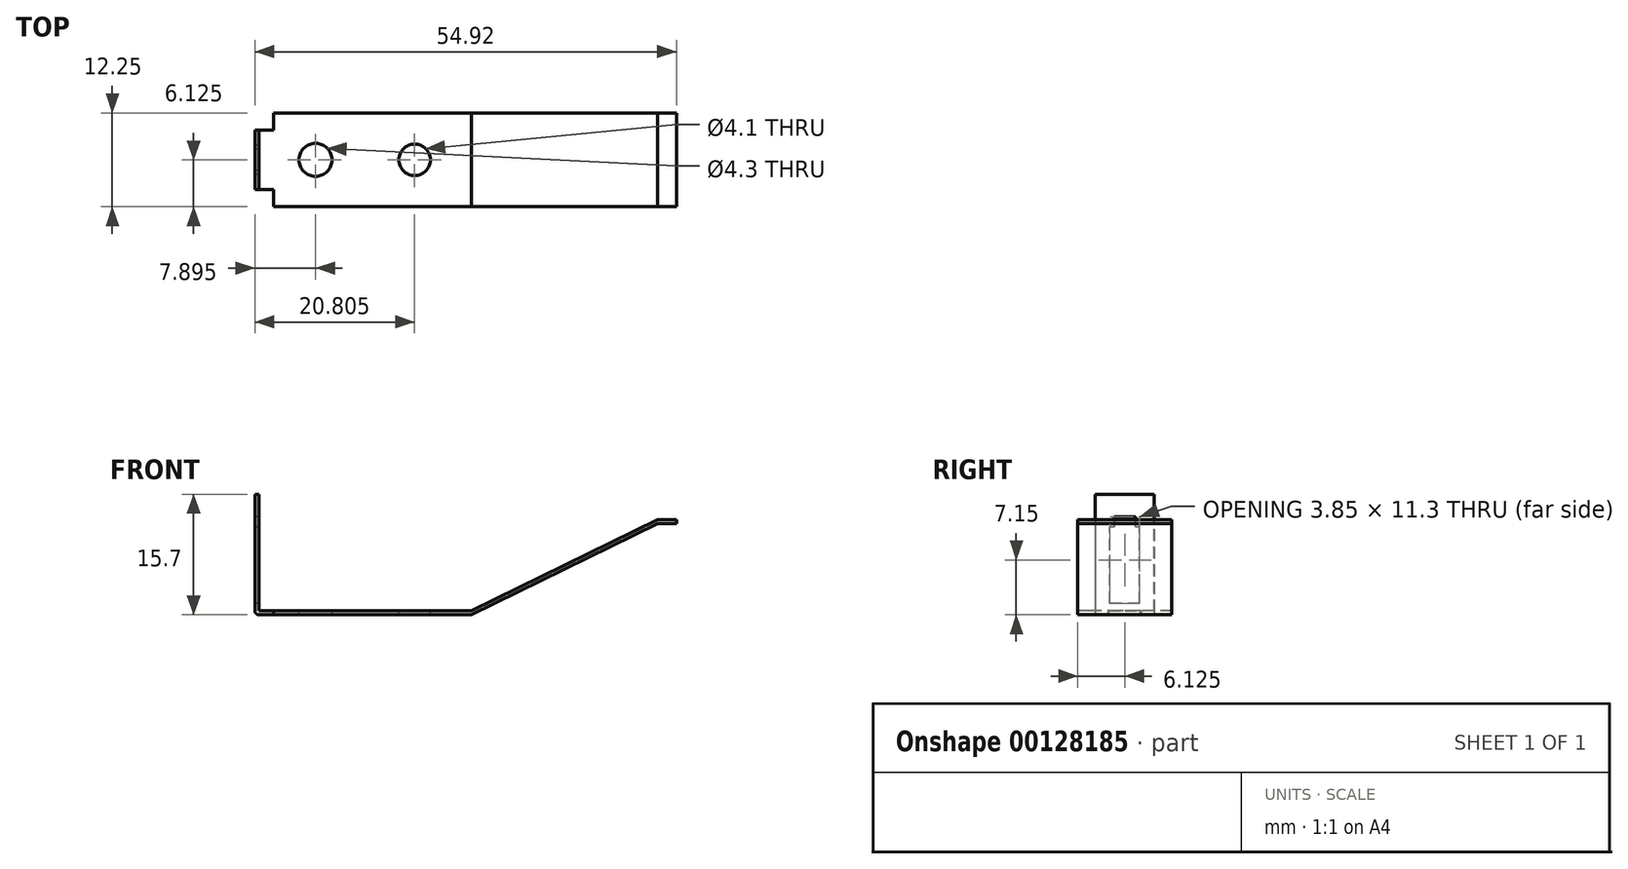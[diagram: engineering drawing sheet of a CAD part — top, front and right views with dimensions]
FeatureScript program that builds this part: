
annotation { "Feature Type Name" : "Feature", "Feature Type Description" : "" }
export const myFeature = defineFeature(function(context is Context, id is Id, definition is map)
    precondition{}
    {
        {
            var Q0;
            Q0=qCreatedBy(makeId("Front.planeOp"),FACE);
            var sketch = newSketch(context, id + "F0", { "sketchPlane" : qUnion([Q0])});
            skLineSegment(sketch, "E0", {"start": v(-12.88, 0) * mm, "end": v(12.88, 0) * mm});
            skLineSegment(sketch, "E1", {"start": v(12.88, 0) * mm, "end": v(37.16, 11.92) * mm});
            skLineSegment(sketch, "E2", {"start": v(37.16, 11.92) * mm, "end": v(39.6, 11.92) * mm});
            skLineSegment(sketch, "E3", {"start": v(-12.88, 0) * mm, "end": v(-12.88, 0.5) * mm});
            skLineSegment(sketch, "E4", {"start": v(-12.88, 0.5) * mm, "end": v(12.88, 0.5) * mm});
            skLineSegment(sketch, "E5", {"start": v(12.88, 0.5) * mm, "end": v(37.16, 12.42) * mm});
            skLineSegment(sketch, "E6", {"start": v(37.16, 12.42) * mm, "end": v(39.6, 12.42) * mm});
            skLineSegment(sketch, "E7", {"start": v(39.6, 12.42) * mm, "end": v(39.6, 11.92) * mm});
            skSolve(sketch);
        }
        {
            var Q0;
            Q0=makeQuery(id+"F0.imprint","IMPRINT",FACE,{"disambiguationData":[TD([[makeQuery(id+"F0.imprint","IMPRINT",EDGE,{"derivedFrom":sQuery(id+"F0.wireOp",EDGE,"E0")}),1.0]])]});
            extrude(context, id + "F1", {"entities" : qUnion([Q0]), "oppositeDirection" : true, "depth" : 12.25 * mm});
        }
        {
            var Q0;
            Q0=qCreatedBy(makeId("Top.planeOp"),FACE);
            var sketch = newSketch(context, id + "F2", { "sketchPlane" : qUnion([Q0])});
            skLineSegment(sketch, "E8", {"start": v(-12.88, 2.28) * mm, "end": v(-15.32, 2.28) * mm});
            skLineSegment(sketch, "E9", {"start": v(-12.88, 2.28) * mm, "end": v(-12.88, 2.28) * mm});
            skLineSegment(sketch, "E10", {"start": v(-12.88, 2.28) * mm, "end": v(-12.88, 9.97) * mm});
            skLineSegment(sketch, "E11", {"start": v(-12.88, 9.97) * mm, "end": v(-15.32, 9.97) * mm});
            skLineSegment(sketch, "E12", {"start": v(-15.32, 9.97) * mm, "end": v(-15.32, 2.28) * mm});
            skSolve(sketch);
        }
        {
            var Q0;
            Q0=makeQuery(id+"F2.imprint","IMPRINT",FACE,{"disambiguationData":[TD([[makeQuery(id+"F2.imprint","IMPRINT",EDGE,{"derivedFrom":sQuery(id+"F2.wireOp",EDGE,"E8")}),-1.0]])]});
            extrude(context, id + "F3", {"entities" : qUnion([Q0]), "operationType" : NewBodyOperationType.ADD, "depth" : 0.5 * mm});
        }
        {
            var Q0;
            Q0=qCreatedBy(makeId("Right.planeOp"),FACE);
            cPlane(context, id + "F4", {"entities" : qUnion([Q0]), "cplaneType" : CPlaneType.OFFSET, "offset" : 15.32 * mm, "oppositeDirection" : true, "width" : 150 * mm, "height" : 150 * mm});
        }
        {
            var Q0;
            Q0=qCreatedBy(id+"F4.planeOp",FACE);
            var sketch = newSketch(context, id + "F5", { "sketchPlane" : qUnion([Q0])});
            skLineSegment(sketch, "E13.0", {"start": v(9.97, 0.5) * mm, "end": v(2.28, 0.5) * mm});
            skLineSegment(sketch, "E13.1", {"start": v(9.97, 0.5) * mm, "end": v(9.97, 0) * mm});
            skLineSegment(sketch, "E13.2", {"start": v(9.97, 0) * mm, "end": v(2.28, 0) * mm});
            skLineSegment(sketch, "E13.3", {"start": v(2.28, 0.5) * mm, "end": v(2.28, 0) * mm});
            skLineSegment(sketch, "E14", {"start": v(9.97, 0) * mm, "end": v(9.97, 16) * mm});
            skLineSegment(sketch, "E15", {"start": v(9.97, 16) * mm, "end": v(2.28, 16) * mm});
            skLineSegment(sketch, "E16", {"start": v(2.28, 16) * mm, "end": v(2.28, 0) * mm});
            skLineSegment(sketch, "E17", {"start": v(8.05, 1.5) * mm, "end": v(4.2, 1.5) * mm});
            skLineSegment(sketch, "E18", {"start": v(4.2, 1.5) * mm, "end": v(4.2, 11.42) * mm});
            skLineSegment(sketch, "E19", {"start": v(8.05, 1.5) * mm, "end": v(8.05, 11.42) * mm});
            skLineSegment(sketch, "E20", {"start": v(8.05, 11.42) * mm, "end": v(4.2, 11.42) * mm});
            skLineSegment(sketch, "E21", {"start": v(7.53, 11.42) * mm, "end": v(7.53, 12.8) * mm});
            skLineSegment(sketch, "E22", {"start": v(7.53, 12.8) * mm, "end": v(4.72, 12.8) * mm});
            skLineSegment(sketch, "E23", {"start": v(4.72, 12.8) * mm, "end": v(4.72, 11.42) * mm});
            skLineSegment(sketch, "E24", {"start": v(9.97, 15.7) * mm, "end": v(2.28, 15.7) * mm});
            skLineSegment(sketch, "E25", {"start": v(9.97, 16) * mm, "end": v(8.97, 16) * mm});
            skLineSegment(sketch, "E26", {"start": v(8.97, 16) * mm, "end": v(8.64, 15.7) * mm});
            skLineSegment(sketch, "E27", {"start": v(8.64, 15.7) * mm, "end": v(8.33, 16) * mm});
            skLineSegment(sketch, "E28", {"start": v(8.33, 16) * mm, "end": v(7.69, 16) * mm});
            skLineSegment(sketch, "E29", {"start": v(7.69, 16) * mm, "end": v(7.26, 15.7) * mm});
            skLineSegment(sketch, "E30", {"start": v(7.26, 15.7) * mm, "end": v(7.05, 16) * mm});
            skLineSegment(sketch, "E31", {"start": v(7.05, 16) * mm, "end": v(6.4, 16) * mm});
            skLineSegment(sketch, "E32", {"start": v(6.4, 16) * mm, "end": v(5.98, 15.7) * mm});
            skLineSegment(sketch, "E33", {"start": v(5.98, 15.7) * mm, "end": v(5.77, 16) * mm});
            skLineSegment(sketch, "E34", {"start": v(5.77, 16) * mm, "end": v(5.13, 16) * mm});
            skLineSegment(sketch, "E35", {"start": v(5.13, 16) * mm, "end": v(4.68, 15.7) * mm});
            skLineSegment(sketch, "E36", {"start": v(4.68, 15.7) * mm, "end": v(4.5, 16) * mm});
            skLineSegment(sketch, "E37", {"start": v(8.97, 16) * mm, "end": v(8.33, 16) * mm});
            skLineSegment(sketch, "E38", {"start": v(4.49, 16) * mm, "end": v(3.85, 16) * mm});
            skLineSegment(sketch, "E39", {"start": v(3.85, 16) * mm, "end": v(3.6, 15.7) * mm});
            skLineSegment(sketch, "E40", {"start": v(3.61, 15.7) * mm, "end": v(3.28, 16) * mm});
            skLineSegment(sketch, "E41", {"start": v(3.28, 16) * mm, "end": v(2.28, 16) * mm});
            skLineSegment(sketch, "E42", {"start": v(9.97, 16) * mm, "end": v(9.97, 15.7) * mm});
            skLineSegment(sketch, "E43", {"start": v(2.28, 15.7) * mm, "end": v(2.28, 16) * mm});
            skLineSegment(sketch, "E44", {"start": v(2.28, 16) * mm, "end": v(3.28, 16) * mm});
            skLineSegment(sketch, "E45", {"start": v(3.28, 16) * mm, "end": v(3.61, 15.7) * mm});
            skLineSegment(sketch, "E46", {"start": v(3.6, 15.7) * mm, "end": v(3.85, 16) * mm});
            skLineSegment(sketch, "E47", {"start": v(3.85, 16) * mm, "end": v(4.49, 16) * mm});
            skLineSegment(sketch, "E48", {"start": v(4.5, 16) * mm, "end": v(4.68, 15.7) * mm});
            skLineSegment(sketch, "E49", {"start": v(4.68, 15.7) * mm, "end": v(5.13, 16) * mm});
            skLineSegment(sketch, "E50", {"start": v(5.13, 16) * mm, "end": v(5.77, 16) * mm});
            skLineSegment(sketch, "E51", {"start": v(5.77, 16) * mm, "end": v(5.98, 15.7) * mm});
            skLineSegment(sketch, "E52", {"start": v(5.98, 15.7) * mm, "end": v(6.4, 16) * mm});
            skLineSegment(sketch, "E53", {"start": v(6.4, 16) * mm, "end": v(7.05, 16) * mm});
            skLineSegment(sketch, "E54", {"start": v(7.05, 16) * mm, "end": v(7.26, 15.7) * mm});
            skLineSegment(sketch, "E55", {"start": v(7.26, 15.7) * mm, "end": v(7.69, 16) * mm});
            skLineSegment(sketch, "E56", {"start": v(7.69, 16) * mm, "end": v(8.33, 16) * mm});
            skLineSegment(sketch, "E57", {"start": v(8.33, 16) * mm, "end": v(8.64, 15.7) * mm});
            skLineSegment(sketch, "E58", {"start": v(8.64, 15.7) * mm, "end": v(8.97, 16) * mm});
            skLineSegment(sketch, "E59", {"start": v(8.97, 16) * mm, "end": v(9.97, 16) * mm});
            skSolve(sketch);
        }
        {
            var Q0;
            {var subQ11=sQuery(id+"F5.wireOp",EDGE,"E13.0");Q0=makeQuery(id+"F5.imprint","IMPRINT",FACE,{"disambiguationData":[TD([[makeQuery(id+"F5.imprint","IMPRINT",EDGE,{"derivedFrom":subQ11}),-1.0]])]});}
            var Q1;
            {var subQ0=sQuery(id+"F5.wireOp",EDGE,"E42");Q1=makeQuery(id+"F5.imprint","IMPRINT",FACE,{"disambiguationData":[TD([[makeQuery(id+"F5.imprint","IMPRINT",EDGE,{"derivedFrom":subQ0}),-1.0]])]});}
            var Q2;
            {var subQ0=sQuery(id+"F5.wireOp",EDGE,"E55");Q2=makeQuery(id+"F5.imprint","IMPRINT",FACE,{"disambiguationData":[TD([[makeQuery(id+"F5.imprint","IMPRINT",EDGE,{"derivedFrom":subQ0}),-1.0]])]});}
            var Q3;
            {var subQ0=sQuery(id+"F5.wireOp",EDGE,"E52");Q3=makeQuery(id+"F5.imprint","IMPRINT",FACE,{"disambiguationData":[TD([[makeQuery(id+"F5.imprint","IMPRINT",EDGE,{"derivedFrom":subQ0}),-1.0]])]});}
            var Q4;
            {var subQ0=sQuery(id+"F5.wireOp",EDGE,"E49");Q4=makeQuery(id+"F5.imprint","IMPRINT",FACE,{"disambiguationData":[TD([[makeQuery(id+"F5.imprint","IMPRINT",EDGE,{"derivedFrom":subQ0}),-1.0]])]});}
            var Q5;
            {var subQ0=sQuery(id+"F5.wireOp",EDGE,"E46");Q5=makeQuery(id+"F5.imprint","IMPRINT",FACE,{"disambiguationData":[TD([[makeQuery(id+"F5.imprint","IMPRINT",EDGE,{"derivedFrom":subQ0}),-1.0]])]});}
            var Q6;
            {var subQ0=sQuery(id+"F5.wireOp",EDGE,"E43");Q6=makeQuery(id+"F5.imprint","IMPRINT",FACE,{"disambiguationData":[TD([[makeQuery(id+"F5.imprint","IMPRINT",EDGE,{"derivedFrom":subQ0}),-1.0]])]});}
            extrude(context, id + "F6", {"entities" : qUnion([Q0, Q1, Q2, Q3, Q4, Q5, Q6]), "operationType" : NewBodyOperationType.ADD, "depth" : 0.5 * mm});
        }
        {
            var Q0;
            Q0=makeQuery(id+"F6.opExtrude","CAP_EDGE",EDGE,{"disambiguationData":[OSD([sQuery(id+"F5.wireOp",EDGE,"E13.0")])],"isStart":false});
            var Q1;
            Q1=makeQuery(id+"F3.opExtrude","CAP_EDGE",EDGE,{"disambiguationData":[OSD([sQuery(id+"F2.wireOp",EDGE,"E12")])],"isStart":true});
            fillet(context, id + "F7", {"entities" : qUnion([Q0, Q1]), "radius" : 0.5 * mm, "tangentPropagation" : true, "allowEdgeOverflow" : false});
        }
        {
            var Q0;
            Q0=makeQuery(id+"F3.boolean.opBoolean","MERGE",FACE,{"derivedFrom":[makeQuery(id+"F1.opExtrude","SWEPT_FACE",FACE,{"disambiguationData":[OSD([sQuery(id+"F0.wireOp",EDGE,"E4")])]}),makeQuery(id+"F3.opExtrude","CAP_FACE",FACE,{"disambiguationData":[OSD([sQuery(id+"F2.wireOp",EDGE,"E8"),sQuery(id+"F2.wireOp",EDGE,"E10"),sQuery(id+"F2.wireOp",EDGE,"E11"),sQuery(id+"F2.wireOp",EDGE,"E12")])],"isStart":false})]});
            var sketch = newSketch(context, id + "F8", { "sketchPlane" : qUnion([Q0])});
            skCircle(sketch, "E60", {"center": v(-7.42, 6.12) * mm, "radius": 2.15 * mm});
            skCircle(sketch, "E61", {"center": v(5.48, 6.12) * mm, "radius": 2.05 * mm});
            skLineSegment(sketch, "E62", {"start": v(-7.42, 12.25) * mm, "end": v(-7.42, 0) * mm, "construction": true});
            skSolve(sketch);
        }
        {
            var Q0;
            Q0=makeQuery(id+"F8.imprint","IMPRINT",FACE,{"disambiguationData":[TD([[makeQuery(id+"F8.imprint","IMPRINT",EDGE,{"derivedFrom":sQuery(id+"F8.wireOp",EDGE,"E60")}),1.0]])]});
            var Q1;
            Q1=makeQuery(id+"F8.imprint","IMPRINT",FACE,{"disambiguationData":[TD([[makeQuery(id+"F8.imprint","IMPRINT",EDGE,{"derivedFrom":sQuery(id+"F8.wireOp",EDGE,"E61")}),1.0]])]});
            extrude(context, id + "F9", {"entities" : qUnion([Q0, Q1]), "operationType" : NewBodyOperationType.REMOVE, "endBound" : BoundingType.THROUGH_ALL, "oppositeDirection" : true, "depth" : 25 * mm});
        }
    });
